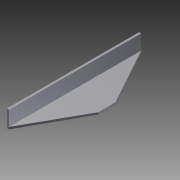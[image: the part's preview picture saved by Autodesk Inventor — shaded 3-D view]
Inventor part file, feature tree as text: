
AUTODESK INVENTOR PART (.ipt)
format: ipt  version: 2012 (Build 160160000, 160)  size: 90,624 bytes
history: native  units: in
note: dims shown in document units (in); Inventor stores cm internally (conversion verified against a paired STEP export)
features: extrude x2, sketch x2
ambient origin geometry x8: Origin, YZ Plane, XZ Plane, XY Plane, X Axis, Y Axis, Z Axis, Center Point
bodies: Solid1 (feature_tree)
feature tree (4):
  extrude  "Extrusion1"  Depth=1.0in
  extrude  "Extrusion4"  Depth=0.125in
  sketch  "Sketch1"  dims[d0=2.0in d1=1.0in]
  sketch  "Sketch2"  dims[d2=0.125in d3=0.125in d4=7.75in d5=0.0in d18=1.0in d19=3.375in d20=3.375in d21=1.0in d22=0.0in]
